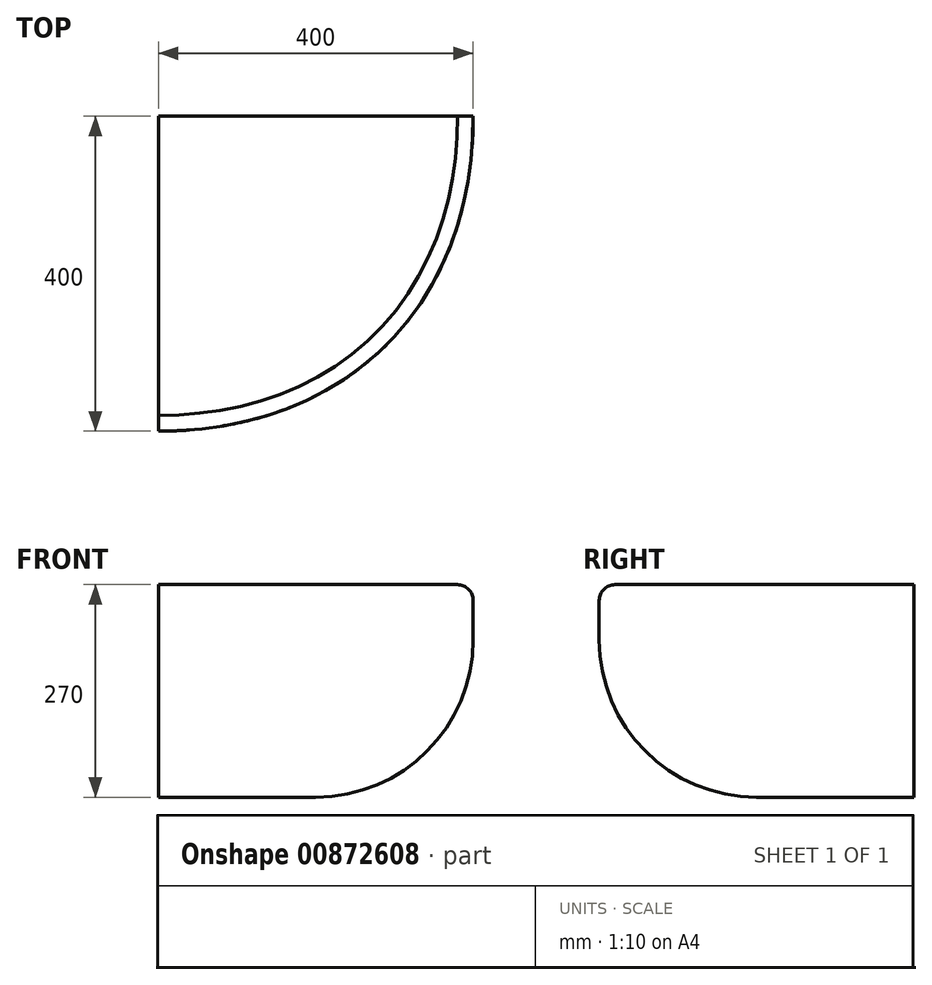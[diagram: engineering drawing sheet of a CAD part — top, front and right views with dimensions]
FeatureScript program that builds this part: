
annotation { "Feature Type Name" : "Feature", "Feature Type Description" : "" }
export const myFeature = defineFeature(function(context is Context, id is Id, definition is map)
    precondition{}
    {
        {
            var Q0;
            Q0=qCreatedBy(makeId("Top.planeOp"),FACE);
            var sketch = newSketch(context, id + "F0", { "sketchPlane" : qUnion([Q0])});
            skLineSegment(sketch, "E0", {"start": v(0, 0) * mm, "end": v(0, -400) * mm});
            skLineSegment(sketch, "E1", {"start": v(0, 0) * mm, "end": v(400, 0) * mm});
            skFitSpline(sketch, "E2", {"points": [v(400, 0) * mm, v(0, -400) * mm], "startDerivative": vector(0, -720) * mm, "endDerivative": vector(-720, 0) * mm});
            skSolve(sketch);
        }
        {
            var Q0;
            Q0 = qSketchRegion(id + "F0", true);
            extrude(context, id + "F1", {"entities" : qUnion([Q0]), "oppositeDirection" : true, "depth" : 270 * mm, "offsetDistance" : 25 * mm});
        }
        {
            var Q0;
            Q0=makeQuery(id+"F1.opExtrude","CAP_EDGE",EDGE,{"disambiguationData":[OSD([sQuery(id+"F0.wireOp",EDGE,"E2")])],"isStart":false});
            fillet(context, id + "F2", {"entities" : qUnion([Q0]), "radius" : 200 * mm, "tangentPropagation" : true, "allowEdgeOverflow" : false});
        }
        {
            var Q0;
            Q0=makeQuery(id+"F1.opExtrude","CAP_EDGE",EDGE,{"disambiguationData":[OSD([sQuery(id+"F0.wireOp",EDGE,"E2")])],"isStart":true});
            fillet(context, id + "F3", {"entities" : qUnion([Q0]), "radius" : 20 * mm, "tangentPropagation" : true, "allowEdgeOverflow" : false});
        }
    });
